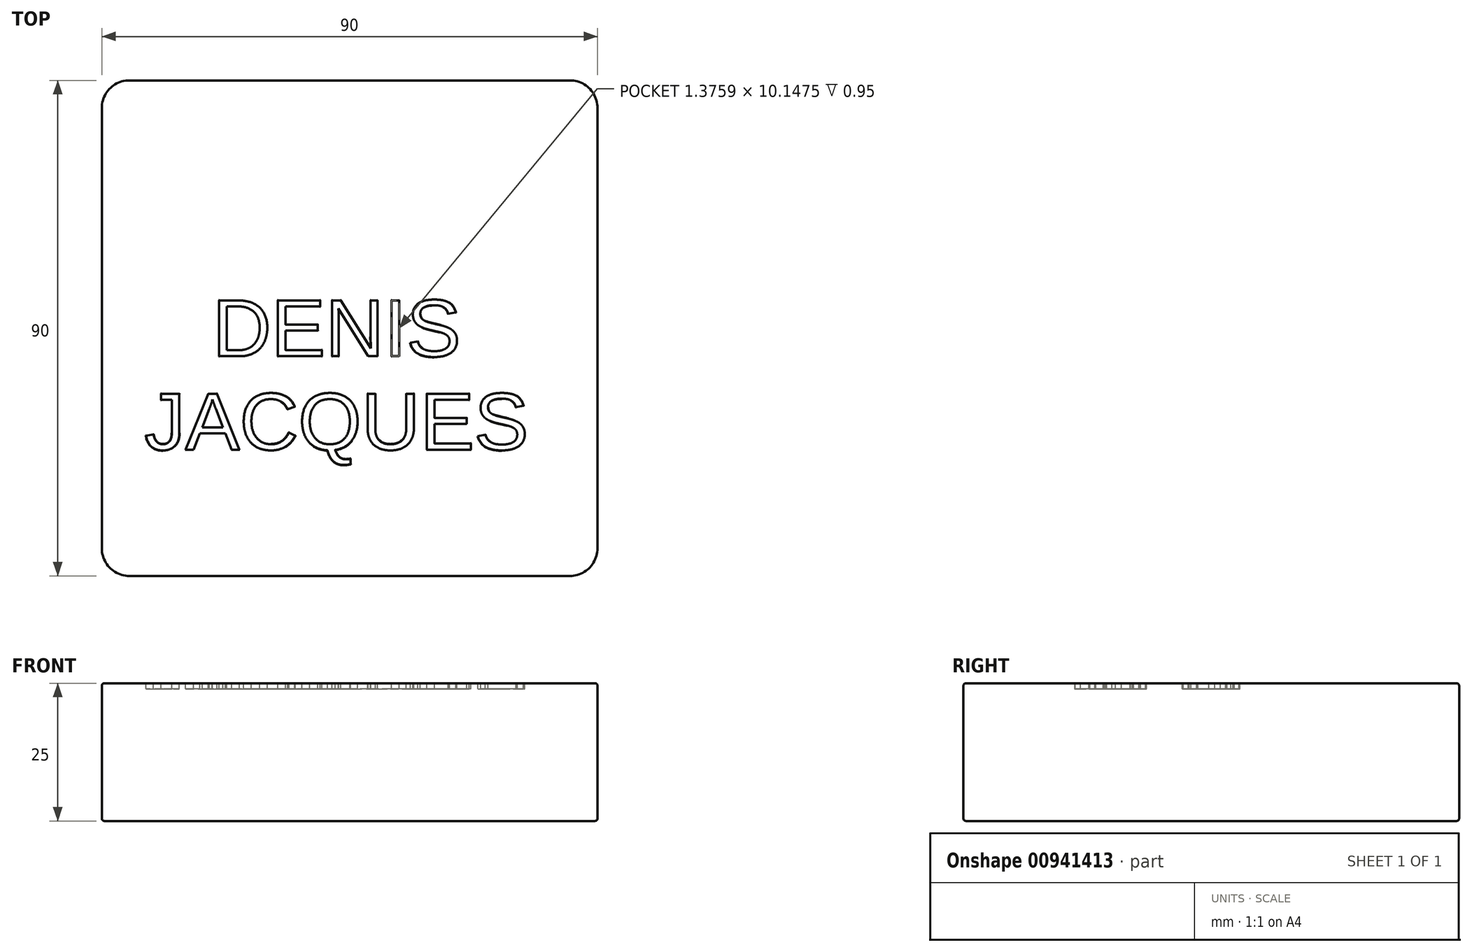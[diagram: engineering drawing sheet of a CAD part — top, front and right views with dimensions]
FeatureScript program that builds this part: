
annotation { "Feature Type Name" : "Feature", "Feature Type Description" : "" }
export const myFeature = defineFeature(function(context is Context, id is Id, definition is map)
    precondition{}
    {
        {
            var Q0;
            Q0=qCreatedBy(makeId("Top.planeOp"),FACE);
            var sketch = newSketch(context, id + "F0", { "sketchPlane" : qUnion([Q0])});
            skLineSegment(sketch, "E0.bottom", {"start": v(-45, 45) * mm, "end": v(45, 45) * mm});
            skLineSegment(sketch, "E0.top", {"start": v(-45, -45) * mm, "end": v(45, -45) * mm});
            skLineSegment(sketch, "E0.left", {"start": v(-45, 45) * mm, "end": v(-45, -45) * mm});
            skLineSegment(sketch, "E0.right", {"start": v(45, 45) * mm, "end": v(45, -45) * mm});
            skSolve(sketch);
        }
        {
            var Q0;
            Q0 = qSketchRegion(id + "F0", true);
            extrude(context, id + "F1", {"entities" : qUnion([Q0]), "depth" : 25 * mm, "offsetDistance" : 25 * mm});
        }
        {
            var Q0;
            Q0=makeQuery(id+"F1.opExtrude","SWEPT_EDGE",EDGE,{"disambiguationData":[OSD([sQuery(id+"F0.wireOp",EDGE,"E0.top"),sQuery(id+"F0.wireOp",EDGE,"E0.left")])]});
            var Q1;
            Q1=makeQuery(id+"F1.opExtrude","SWEPT_EDGE",EDGE,{"disambiguationData":[OSD([sQuery(id+"F0.wireOp",EDGE,"E0.top"),sQuery(id+"F0.wireOp",EDGE,"E0.right")])]});
            var Q2;
            Q2=makeQuery(id+"F1.opExtrude","SWEPT_EDGE",EDGE,{"disambiguationData":[OSD([sQuery(id+"F0.wireOp",EDGE,"E0.bottom"),sQuery(id+"F0.wireOp",EDGE,"E0.right")])]});
            var Q3;
            Q3=makeQuery(id+"F1.opExtrude","SWEPT_EDGE",EDGE,{"disambiguationData":[OSD([sQuery(id+"F0.wireOp",EDGE,"E0.bottom"),sQuery(id+"F0.wireOp",EDGE,"E0.left")])]});
            fillet(context, id + "F2", {"entities" : qUnion([Q0, Q1, Q2, Q3]), "radius" : 5 * mm, "tangentPropagation" : true, "allowEdgeOverflow" : false});
        }
        {
            var Q0;
            Q0=makeQuery(id+"F1.opExtrude","CAP_FACE",FACE,{"disambiguationData":[OSD([sQuery(id+"F0.wireOp",EDGE,"E0.bottom"),sQuery(id+"F0.wireOp",EDGE,"E0.top"),sQuery(id+"F0.wireOp",EDGE,"E0.left"),sQuery(id+"F0.wireOp",EDGE,"E0.right")])],"isStart":false});
            var sketch = newSketch(context, id + "F3", { "sketchPlane" : qUnion([Q0])});
            skText(sketch, "E1", { "text": "   DENIS\nJACQUES", "fontName": "Arimo-Regular.ttf"});
            const initialGuessF3  = {"E1": [-0.0372, -0.0051, 1, 0, 0.01062]};
            skSetInitialGuess(sketch, initialGuessF3);
            skSolve(sketch);
        }
        {
            var Q0;
            Q0 = qSketchRegion(id + "F3", true);
            extrude(context, id + "F4", {"entities" : qUnion([Q0]), "operationType" : NewBodyOperationType.REMOVE, "oppositeDirection" : true, "depth" : 1 * mm, "offsetDistance" : 25 * mm});
        }
        {
            var Q0;
            Q0=makeQuery(id+"F1.opExtrude","SWEPT_FACE",FACE,{"disambiguationData":[OSD([sQuery(id+"F0.wireOp",EDGE,"E0.top")])]});
            fillet(context, id + "F5", {"entities" : qUnion([Q0]), "radius" : .5 * mm, "tangentPropagation" : true, "rho" : 0.5, "crossSection" : FilletCrossSection.CONIC, "allowEdgeOverflow" : false});
        }
        {
            var Q0;
            {var subQ0=sQuery(id+"F0.wireOp",EDGE,"E0.left");var subQ1=sQuery(id+"F0.wireOp",EDGE,"E0.bottom");var subQ2=sQuery(id+"F0.wireOp",EDGE,"E0.top");var subQ3=sQuery(id+"F0.wireOp",EDGE,"E0.right");Q0=makeQuery(id+"F4.boolean.opBoolean","SPLIT",FACE,{"disambiguationData":[TD([makeQuery(id+"F1.opExtrude","SWEPT_FACE",FACE,{"disambiguationData":[OSD([subQ1])]})])],"derivedFrom":makeQuery(id+"F1.opExtrude","CAP_FACE",FACE,{"disambiguationData":[OSD([subQ1,subQ2,subQ0,subQ3])],"isStart":false})});}
            fillet(context, id + "F6", {"entities" : qUnion([Q0]), "radius" : 0.05 * mm, "tangentPropagation" : true, "allowEdgeOverflow" : false});
        }
    });
